# Revit family: LAMP_HANCE 48V 500
name_source: partatom
category: Luminarias
revit_build: Autodesk Revit 2015 (Build: 20140606_1530(x64)
units: mm (PartAtom-declared; Revit-internal decimal feet)

## types (18) — shared parameters
CRI = 80
Comentarios de tipo = Availability of tilting between 0º and 90º, rotation between 0º and 355º and change ring color when placed in a project.
Diameter = 40 mm  [stored 0.131234 ft]
Elevación por defecto = 1219 mm
Fabricante = LAMP
Gear = Electronic
Height = 78 mm  [stored 0.255906 ft]
IEE = A+
Installation instructions = https://www.lamp.es
Insulation class = III
LED Lifetime = 50.000 L90
Lamp = HIGH POWER LED
Last update = 18/03/2019
Luminaire type = Indoor - Spotlight
MacAdam = 5
Manufacturer URL = http://www.lamp.es
Manufacturer country = Spain
Manufacturer name = LAMP
Model explanation = Availability of tilting between 0º and 90º, rotation between 0º and 355º and change ring color when placed in a project.
Plum = 6 W
Power = 5 W
Power Supply = 48V DC
Product URL = https://www.lamp.es
Product datasheet = http://www.lamp.es
Protection rating = IP20
Type = HIGH POWER CREE
Weight = 0.15 kg

## per-type parameters (varying)
| type | Descripción | Efficacy | Finish | Initial color | Initial intensity | Material tija | Modelo | Photometric web file | Product code |
| 314LM 2700 SPOT BLACK | HANCE TRACK 48 500 VWW SP BK. | 51 lm/W | RAL9011 textured | 2700 K | 314 lm | LAMP_Aluminio Hance Negro | HS1TL05SP827NBB | Cuerpo Hance 48V BASE 500 (tilting) : 314LM 2700 SPOT BLACK | HS1TL05SP827NBB |
| 314LM 2700 SPOT WHITE | HANCE TRACK 48 500 VWW SP WH. | 51 lm/W | RAL9010 textured | 2700 K | 314 lm | LAMP_Aluminio Hance Blanco | HS1TL05SP827NBW | Cuerpo Hance 48V BASE 500 (tilting) : 314LM 2700 SPOT WHITE | HS1TL05SP827NBW |
| 314LM 3000 SPOT BLACK | HANCE TRACK 48 500 WW SP BK. | 51 lm/W | RAL9011 textured | 3000 K | 314 lm | LAMP_Aluminio Hance Negro | HS1TL05SP830NBB | Cuerpo Hance 48V BASE 500 (tilting) : 314LM 3000 SPOT BLACK | HS1TL05SP830NBB |
| 314LM 3000 SPOT WHITE | HANCE TRACK 48 500 WW SP WH. | 51 lm/W | RAL9010 textured | 3000 K | 314 lm | LAMP_Aluminio Hance Blanco | HS1TL05SP830NBW | Cuerpo Hance 48V BASE 500 (tilting) : 314LM 3000 SPOT WHITE | HS1TL05SP830NBW |
| 339LM 4000 SPOT BLACK | HANCE TRACK 48 500 NW SP BK. | 55 lm/W | RAL9011 textured | 4000 K | 339 lm | LAMP_Aluminio Hance Negro | HS1TL05SP840NBB | Cuerpo Hance 48V BASE 500 (tilting) : 339LM 4000 SPOT BLACK | HS1TL05SP840NBB |
| 339LM 4000 SPOT WHITE | HANCE TRACK 48 500 NW SP WH. | 55 lm/W | RAL9010 textured | 4000 K | 339 lm | LAMP_Aluminio Hance Blanco | HS1TL05SP840NBW | Cuerpo Hance 48V BASE 500 (tilting) : 339LM 4000 SPOT WHITE | HS1TL05SP840NBW |
| 330LM 2700 MEDIUM FLOOD BLACK | HANCE TRACK 48 500 VWW MFL BK. | 54 lm/W | RAL9011 textured | 2700 K | 330 lm | LAMP_Aluminio Hance Negro | HS1TL05MF827NBB | Cuerpo Hance 48V BASE 500 (tilting) : 330LM 2700 MEDIUM FLOOD BLACK | HS1TL05MF827NBB |
| 330LM 2700 MEDIUM FLOOD WHITE | HANCE TRACK 48 500 VWW MFL WH. | 54 lm/W | RAL9010 textured | 2700 K | 330 lm | LAMP_Aluminio Hance Blanco | HS1TL05MF827NBW | Cuerpo Hance 48V BASE 500 (tilting) : 330LM 2700 MEDIUM FLOOD WHITE | HS1TL05MF827NBW |
| 330LM 3000 MEDIUM FLOOD BLACK | HANCE TRACK 48 500 WW MFL BK. | 54 lm/W | RAL9011 textured | 3000 K | 330 lm | LAMP_Aluminio Hance Negro | HS1TL05MF830NBB | Cuerpo Hance 48V BASE 500 (tilting) : 330LM 3000 MEDIUM FLOOD BLACK | HS1TL05MF830NBB |
| 330LM 3000 MEDIUM FLOOD WHITE | HANCE TRACK 48 500 WW MFL WH. | 54 lm/W | RAL9010 textured | 3000 K | 330 lm | LAMP_Aluminio Hance Blanco | HS1TL05MF830NBW | Cuerpo Hance 48V BASE 500 (tilting) : 330LM 3000 MEDIUM FLOOD WHITE | HS1TL05MF830NBW |
| 356LM 4000 MEDIUM FLOOD BLACK | HANCE TRACK 48 500 NW MFL BK. | 58 lm/W | RAL9011 textured | 4000 K | 356 lm | LAMP_Aluminio Hance Negro | HS1TL05MF840NBB | Cuerpo Hance 48V BASE 500 (tilting) : 356LM 4000 MEDIUM FLOOD BLACK | HS1TL05MF840NBB |
| 356LM 4000 MEDIUM FLOOD WHITE | HANCE TRACK 48 500 NW MFL WH. | 58 lm/W | RAL9010 textured | 4000 K | 356 lm | LAMP_Aluminio Hance Blanco | HS1TL05MF840NBW | Cuerpo Hance 48V BASE 500 (tilting) : 356LM 4000 MEDIUM FLOOD WHITE | HS1TL05MF840NBW |
| 324LM 2700 FLOOD BLACK | HANCE TRACK 48 500 VWW FL BK. | 53 lm/W | RAL9011 textured | 2700 K | 324 lm | LAMP_Aluminio Hance Negro | HS1TL05FL827NBB | Cuerpo Hance 48V BASE 500 (tilting) : 324LM 2700 FLOOD BLACK | HS1TL05FL827NBB |
| 324LM 2700 FLOOD WHITE | HANCE TRACK 48 500 VWW FL WH. | 53 lm/W | RAL9010 textured | 2700 K | 324 lm | LAMP_Aluminio Hance Blanco | HS1TL05FL827NBW | Cuerpo Hance 48V BASE 500 (tilting) : 324LM 2700 FLOOD WHITE | HS1TL05FL827NBW |
| 324LM 3000 FLOOD BLACK | HANCE TRACK 48 500 WW FL BK. | 53 lm/W | RAL9011 textured | 3000 K | 324 lm | LAMP_Aluminio Hance Negro | HS1TL05FL830NBB | Cuerpo Hance 48V BASE 500 (tilting) : 324LM 3000 FLOOD BLACK | HS1TL05FL830NBB |
| 324LM 3000 FLOOD WHITE | HANCE TRACK 48 500 WW FL WH. | 53 lm/W | RAL9010 textured | 3000 K | 324 lm | LAMP_Aluminio Hance Blanco | HS1TL05FL830NBW | Cuerpo Hance 48V BASE 500 (tilting) : 324LM 3000 FLOOD WHITE | HS1TL05FL830NBW |
| 349LM 4000 FLOOD BLACK | HANCE TRACK 48 500 NW FL BK. | 57 lm/W | RAL9011 textured | 4000 K | 349 lm | LAMP_Aluminio Hance Negro | HS1TL05FL840NBB | Cuerpo Hance 48V BASE 500 (tilting) : 349LM 4000 FLOOD BLACK | HS1TL05FL840NBB |
| 349LM 4000 FLOOD WHITE | HANCE TRACK 48 500 NW FL WH. | 57 lm/W | RAL9010 textured | 4000 K | 349 lm | LAMP_Aluminio Hance Blanco | HS1TL05FL840NBW | Cuerpo Hance 48V BASE 500 (tilting) : 349LM 4000 FLOOD WHITE | HS1TL05FL840NBW |

note: [stored X ft] marks values corroborated as IEEE doubles in the binary element streams (Revit-internal decimal feet)
